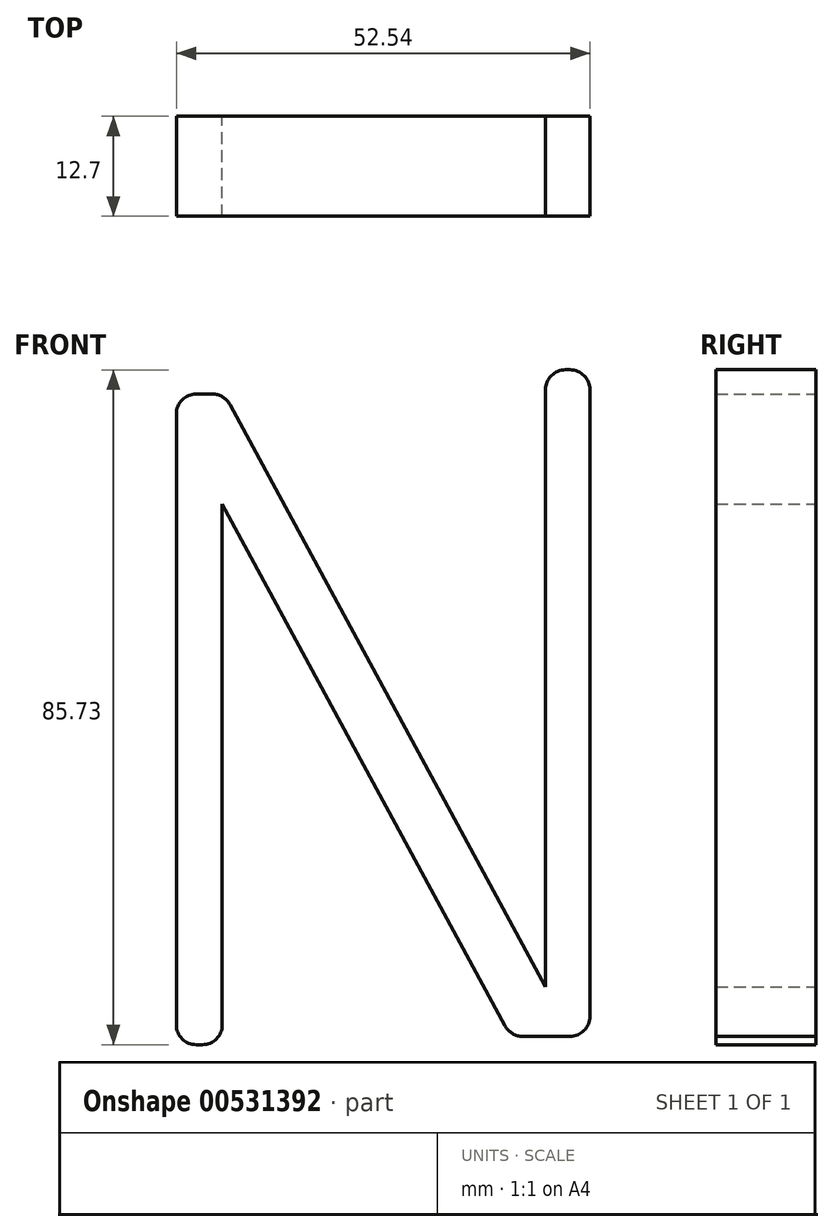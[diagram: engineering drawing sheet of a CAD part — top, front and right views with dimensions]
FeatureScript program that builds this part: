
annotation { "Feature Type Name" : "Feature", "Feature Type Description" : "" }
export const myFeature = defineFeature(function(context is Context, id is Id, definition is map)
    precondition{}
    {
        {
            var Q0;
            Q0=qCreatedBy(makeId("Front.planeOp"),FACE);
            var sketch = newSketch(context, id + "F0", { "sketchPlane" : qUnion([Q0])});
            skLineSegment(sketch, "E0", {"start": v(-15.06, 45.31) * mm, "end": v(-15.06, -37.34) * mm});
            skLineSegment(sketch, "E1", {"start": v(-8.98, 45.31) * mm, "end": v(-15.06, 45.31) * mm});
            skLineSegment(sketch, "E2", {"start": v(-8.98, 45.31) * mm, "end": v(31.84, -29.97) * mm});
            skLineSegment(sketch, "E3", {"start": v(-15.06, -37.34) * mm, "end": v(-9.22, -37.34) * mm});
            skLineSegment(sketch, "E4", {"start": v(-9.22, -37.34) * mm, "end": v(-9.22, 31.33) * mm});
            skLineSegment(sketch, "E5", {"start": v(-9.22, 31.33) * mm, "end": v(27.44, -36.3) * mm});
            skPoint(sketch, "E6.start.orphan", {"position": v(44.93, -29.97) * mm});
            skPoint(sketch, "E7.orphan", {"position": v(24, -29.97) * mm});
            skLineSegment(sketch, "E8", {"start": v(27.44, -36.3) * mm, "end": v(37.48, -36.3) * mm});
            skLineSegment(sketch, "E9", {"start": v(37.48, -36.3) * mm, "end": v(37.48, 48.4) * mm});
            skLineSegment(sketch, "E10", {"start": v(31.84, -29.97) * mm, "end": v(31.84, 48.4) * mm});
            skLineSegment(sketch, "E11", {"start": v(31.84, 48.4) * mm, "end": v(37.48, 48.4) * mm});
            skSolve(sketch);
        }
        {
            var Q0;
            Q0=makeQuery(id+"F0.imprint","IMPRINT",FACE,{"disambiguationData":[TD([[makeQuery(id+"F0.imprint","IMPRINT",EDGE,{"derivedFrom":sQuery(id+"F0.wireOp",EDGE,"E0")}),1.0]])]});
            extrude(context, id + "F1", {"entities" : qUnion([Q0]), "endBound" : BoundingType.SYMMETRIC, "depth" : 12.7 * mm, "offsetDistance" : 25.4 * mm});
        }
        {
            var Q0;
            Q0=makeQuery(id+"F1.opExtrude","SWEPT_EDGE",EDGE,{"disambiguationData":[OSD([sQuery(id+"F0.wireOp",EDGE,"E0"),sQuery(id+"F0.wireOp",EDGE,"E3")])]});
            var Q1;
            Q1=makeQuery(id+"F1.opExtrude","SWEPT_EDGE",EDGE,{"disambiguationData":[OSD([sQuery(id+"F0.wireOp",EDGE,"E9"),sQuery(id+"F0.wireOp",EDGE,"E11")])]});
            var Q2;
            Q2=makeQuery(id+"F1.opExtrude","SWEPT_EDGE",EDGE,{"disambiguationData":[OSD([sQuery(id+"F0.wireOp",EDGE,"E0"),sQuery(id+"F0.wireOp",EDGE,"E1")])]});
            var Q3;
            Q3=makeQuery(id+"F1.opExtrude","SWEPT_EDGE",EDGE,{"disambiguationData":[OSD([sQuery(id+"F0.wireOp",EDGE,"E10"),sQuery(id+"F0.wireOp",EDGE,"E11")])]});
            var Q4;
            Q4=makeQuery(id+"F1.opExtrude","SWEPT_EDGE",EDGE,{"disambiguationData":[OSD([sQuery(id+"F0.wireOp",EDGE,"E3"),sQuery(id+"F0.wireOp",EDGE,"E4")])]});
            var Q5;
            Q5=makeQuery(id+"F1.opExtrude","SWEPT_EDGE",EDGE,{"disambiguationData":[OSD([sQuery(id+"F0.wireOp",EDGE,"E8"),sQuery(id+"F0.wireOp",EDGE,"E9")])]});
            var Q6;
            Q6=makeQuery(id+"F1.opExtrude","SWEPT_EDGE",EDGE,{"disambiguationData":[OSD([sQuery(id+"F0.wireOp",EDGE,"E5"),sQuery(id+"F0.wireOp",EDGE,"E8")])]});
            var Q7;
            Q7=makeQuery(id+"F1.opExtrude","SWEPT_EDGE",EDGE,{"disambiguationData":[OSD([sQuery(id+"F0.wireOp",EDGE,"E1"),sQuery(id+"F0.wireOp",EDGE,"E2")])]});
            fillet(context, id + "F2", {"entities" : qUnion([Q0, Q1, Q2, Q3, Q4, Q5, Q6, Q7]), "radius" : 2.54 * mm, "tangentPropagation" : true, "allowEdgeOverflow" : false});
        }
    });
